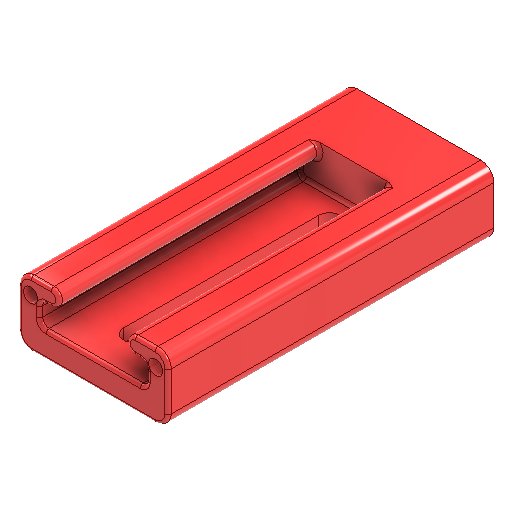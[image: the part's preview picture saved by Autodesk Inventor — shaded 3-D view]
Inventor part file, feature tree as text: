
AUTODESK INVENTOR PART (.ipt)
format: ipt  version: 2023 (Build 270158000, 158)  size: 344,576 bytes
history: native  units: in
note: dims shown in document units (in); Inventor stores cm internally (conversion verified against a paired STEP export)
features: extrude x6, sketch x6, projected_geometry x4, fillet x3, other x3, reference x1
ambient origin geometry x8: Origin, YZ Plane, XZ Plane, XY Plane, X Axis, Y Axis, Z Axis, Center Point
bodies: Solid1 (feature_tree)
feature tree (23):
  extrude  "Extrusion1"  Depth=0.3937in
  extrude  "Extrusion2"  Depth=0.1575in
  extrude  "Extrusion3"  Depth=0.0787in
  extrude  "Extrusion4"  Depth=0.1575in TaperAngle=0.0deg
  extrude  "Extrusion5"  Depth=0.5079in
  extrude  "Extrusion6"  Depth=0.0197in
  fillet  "Fillet1"  Radius=0.128in
  fillet  "Fillet2"  Radius=0.0394in
  fillet  "Fillet3"  Radius=1.5748in
  sketch  "Sketch1"  dims[d0=0.9055in d1=0.3937in]
  reference  "Reference1"
  sketch  "Sketch2"  dims[d2=0.1575in d3=0.1575in]
  projected_geometry  "Projected Loop1"
  sketch  "Sketch3"  dims[d4=0.0787in d5=0.0787in]
  projected_geometry  "Projected Loop2"
  sketch  "Sketch4"  dims[d6=0.2362in d7=0.0in d8=0.1575in d9=0.0in]
  projected_geometry  "Projected Loop3"
  sketch  "Sketch5"  dims[d10=0.0492in d11=0.5079in]
  sketch  "Sketch6"  dims[d12=0.1575in d13=0.128in d14=0.128in d15=0.0394in d16=1.5748in d17=0.0in d18=0.0866in d19=0.0866in d20=0.0in d21=0.0in d22=0.0984in d23=0.2953in d24=0.5413in d25=0.2461in d26=0.0787in d27=0.0in d28=0.0846in d29=0.0in d30=0.0in d31=0.0197in d32=0.0197in d33=0.0197in d34=0.0108in d35=0.0108in]
  projected_geometry  "Projected Loop4"
  other  "<userpath>\Documents\Github\Acoustifly\CAD\1_Col_Print\Assembly.iam"
  other  "Assembly.iam"
  other  "Base:1"
